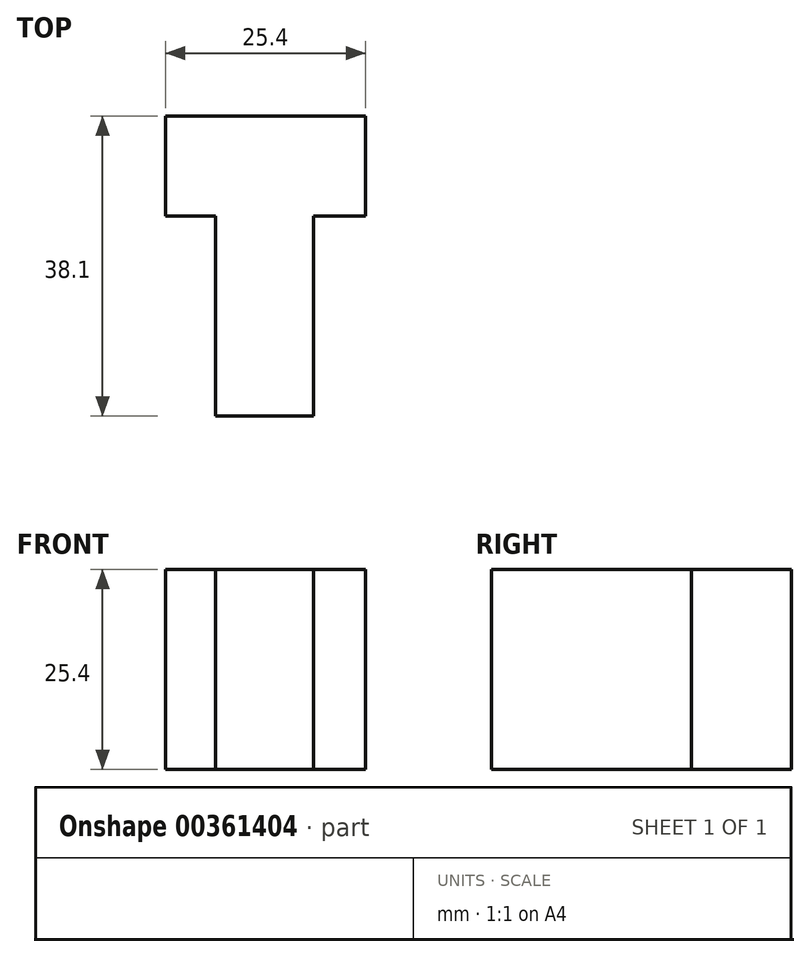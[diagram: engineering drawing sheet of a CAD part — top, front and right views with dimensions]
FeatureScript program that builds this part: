
annotation { "Feature Type Name" : "Feature", "Feature Type Description" : "" }
export const myFeature = defineFeature(function(context is Context, id is Id, definition is map)
    precondition{}
    {
        {
            var Q0;
            Q0=qCreatedBy(makeId("Top.planeOp"),FACE);
            var sketch = newSketch(context, id + "F0", { "sketchPlane" : qUnion([Q0])});
            skLineSegment(sketch, "E0", {"start": v(0, 0) * mm, "end": v(0, 25.4) * mm});
            skLineSegment(sketch, "E1", {"start": v(0, 25.4) * mm, "end": v(-6.35, 25.4) * mm});
            skLineSegment(sketch, "E2", {"start": v(-6.35, 25.4) * mm, "end": v(-6.35, 38.1) * mm});
            skLineSegment(sketch, "E3", {"start": v(-6.35, 38.1) * mm, "end": v(19.05, 38.1) * mm});
            skLineSegment(sketch, "E4", {"start": v(19.05, 38.1) * mm, "end": v(19.05, 25.4) * mm});
            skLineSegment(sketch, "E5", {"start": v(19.05, 25.4) * mm, "end": v(12.46, 25.4) * mm});
            skLineSegment(sketch, "E6", {"start": v(12.46, 25.4) * mm, "end": v(12.46, 0) * mm});
            skLineSegment(sketch, "E7", {"start": v(0, 0) * mm, "end": v(12.46, 0) * mm});
            skSolve(sketch);
        }
        {
            var Q0;
            Q0 = qSketchRegion(id + "F0", true);
            extrude(context, id + "F1", {"entities" : qUnion([Q0]), "oppositeDirection" : true, "depth" : 25.4 * mm});
        }
    });
